# Revit family: Bonnet_chandelier_SC91
name_source: partatom
category: Furniture
units: mm (PartAtom-declared; Revit-internal decimal feet)

## family parameters
Always vertical = Yes
Cut with Voids When Loaded = No
Enable Cutting in Views = No
OmniClass Number = 23.40.20.00
OmniClass Title = General Furniture and Specialties
Render Appearance Source = Family Geometry
Room Calculation Point = No
Shared = No
Work Plane-Based = No

## types (1)
- Bonnet_chandelier_SC91
    Cord = &tradition Textile Black
    Default Elevation = 0 mm  [stored 0 ft]
    Depth = 100cm/39,37in
    Design = Space Copenhagen
    Design Year = 2024
    Height = 40cm/15,75in
    Inner Shade = &tradition Powder Coated Steel White 9010 Semi Matt Finish
    Manufacturer = &Tradition
    Model = SC91 Bonnet
    Outer shade and wall bracket = &tradition Powder Coated Metal black matt RAL 9011
    Packaging dimensions & weight = Please see product fact sheet available from download page on website
    Stem and canopy = &tradition Powder Coated Metal black matt RAL 9011
    Type Comments = Bonnet
    URL = https://www.andtradition.com
    Variation = Please visit our website to see available colours and finishes.
    Width = 140cm/55,12in

note: [stored X ft] marks values corroborated as IEEE doubles in the binary element streams (Revit-internal decimal feet)

## geometry (parser evidence)
native form markers: Sweep x3
no freeform markers — native parametric forms only
